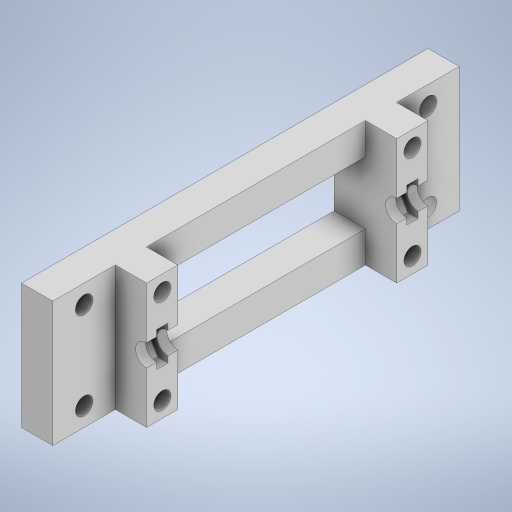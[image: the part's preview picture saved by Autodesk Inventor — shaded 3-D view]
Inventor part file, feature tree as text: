
AUTODESK INVENTOR PART (.ipt)
format: ipt  version: 2023 (Build 270158000, 158)  size: 375,296 bytes
history: native  units: mm
features: extrude x7, sketch x7, plane x2, mirror x1
ambient origin geometry x8: Origin, YZ Plane, XZ Plane, XY Plane, X Axis, Y Axis, Z Axis, Center Point
bodies: Solid1 (feature_tree)
feature tree (17):
  extrude  "Extrusion1"  Depth=5.0mm
  extrude  "Extrusion2"  Depth=15.0mm
  extrude  "Extrusion3"  Depth=35.0mm
  extrude  "Extrusion4"  Depth=10.0mm
  extrude  "Extrusion5"  Depth=10.0mm
  extrude  "Extrusion6"  Depth=200.0mm TaperAngle=0.0deg
  plane  "Work Plane1"
  extrude  "Extrusion7"  Depth=5.0mm
  plane  "Work Plane2"
  mirror  "Mirror1"
  sketch  "Sketch1"  dims[d0=5.0mm d1=5.0mm]
  sketch  "Sketch2"  dims[d2=5.0mm d3=15.0mm]
  sketch  "Sketch3"  dims[d4=15.0mm d5=35.0mm]
  sketch  "Sketch4"  dims[d6=20.0mm d7=0.0mm d8=10.0mm]
  sketch  "Sketch5"  dims[d9=10.0mm d10=10.0mm]
  sketch  "Sketch6"  dims[d11=3.5mm d12=200.0mm d13=0.0mm]
  sketch  "Sketch7"  dims[d14=5.0mm d15=5.0mm d16=20.0mm d17=0.0mm d18=10.0mm d19=10.0mm d20=3.0mm d21=3.0mm d22=5.0mm d23=5.0mm d24=5.0mm d25=5.0mm d26=3.0mm d27=3.0mm d28=2.75mm d29=2.75mm d30=2.75mm d31=2.75mm d32=5.0mm d33=0.0mm d34=2.5mm d35=2.5mm d36=2.5mm d37=2.5mm d38=2.5mm d39=2.5mm d40=2.5mm d41=2.5mm d42=2.7mm d43=2.7mm d44=2.7mm d45=2.7mm d46=15.0mm d47=0.0mm d48=4.0mm d49=4.0mm d50=4.0mm d51=4.0mm d52=5.0mm d53=0.0mm d54=2.75mm d55=0.0mm d56=10.0mm d57=20.0mm d58=1.8mm d59=0.0mm]
